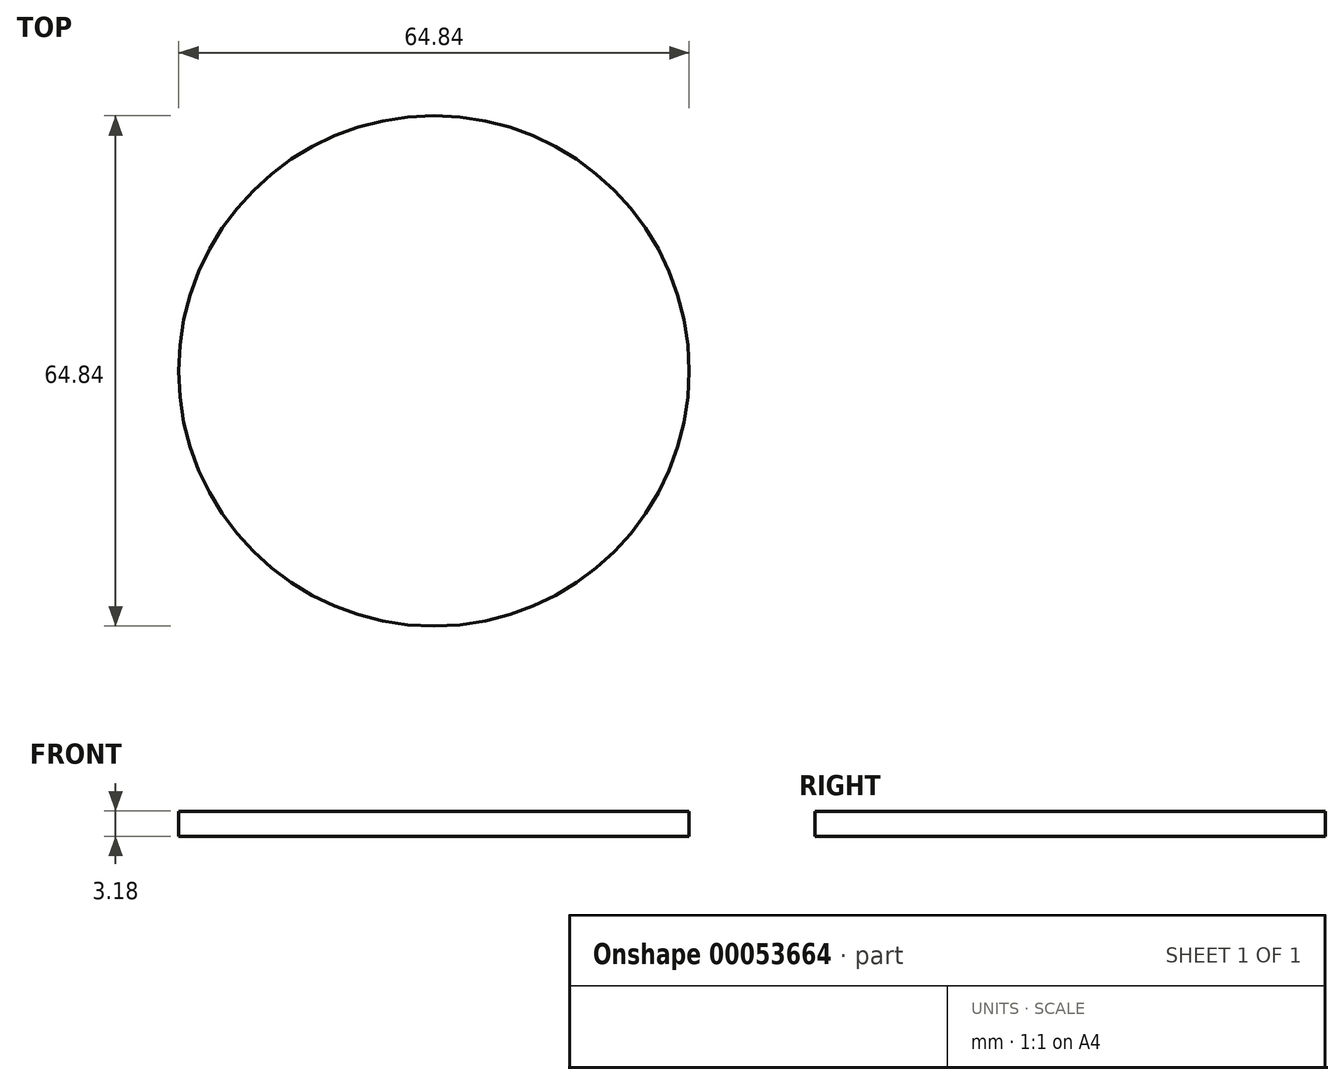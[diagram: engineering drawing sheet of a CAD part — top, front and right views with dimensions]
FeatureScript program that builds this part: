
annotation { "Feature Type Name" : "Feature", "Feature Type Description" : "" }
export const myFeature = defineFeature(function(context is Context, id is Id, definition is map)
    precondition{}
    {
        {
            var Q0;
            Q0=qCreatedBy(makeId("Top.planeOp"),FACE);
            var sketch = newSketch(context, id + "F0", { "sketchPlane" : qUnion([Q0])});
            skCircle(sketch, "E0", {"center": v(0, 0) * mm, "radius": 32.42 * mm});
            skSolve(sketch);
        }
        {
            var Q0;
            Q0 = qSketchRegion(id + "F0", true);
            extrude(context, id + "F1", {"entities" : qUnion([Q0]), "depth" : 3.17 * mm});
        }
    });
